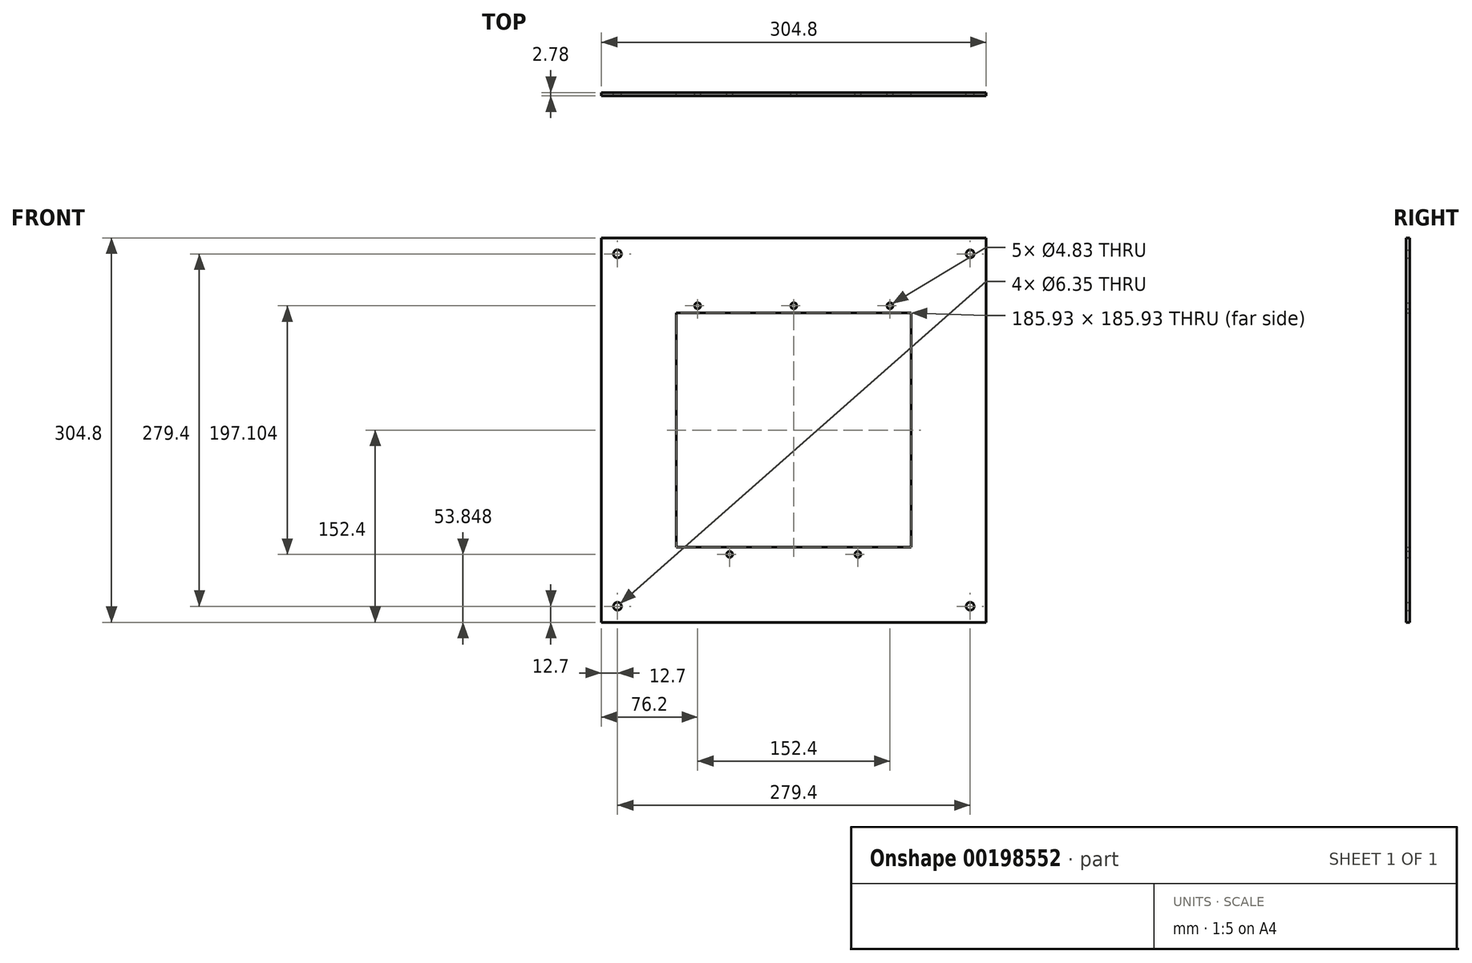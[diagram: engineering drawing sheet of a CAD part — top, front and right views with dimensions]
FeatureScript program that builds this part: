
annotation { "Feature Type Name" : "Feature", "Feature Type Description" : "" }
export const myFeature = defineFeature(function(context is Context, id is Id, definition is map)
    precondition{}
    {
        {
            var Q0;
            Q0=qCreatedBy(makeId("Front.planeOp"),FACE);
            var sketch = newSketch(context, id + "F0", { "sketchPlane" : qUnion([Q0])});
            skLineSegment(sketch, "E0.bottom", {"start": v(-152.4, 152.4) * mm, "end": v(152.4, 152.4) * mm});
            skLineSegment(sketch, "E0.top", {"start": v(-152.4, -152.4) * mm, "end": v(152.4, -152.4) * mm});
            skLineSegment(sketch, "E0.left", {"start": v(-152.4, 152.4) * mm, "end": v(-152.4, -152.4) * mm});
            skLineSegment(sketch, "E0.right", {"start": v(152.4, 152.4) * mm, "end": v(152.4, -152.4) * mm});
            skPoint(sketch, "E0.middle", {"position": v(0, 0) * mm});
            skLineSegment(sketch, "E1.bottom", {"start": v(-92.96, 92.96) * mm, "end": v(92.96, 92.96) * mm});
            skLineSegment(sketch, "E1.top", {"start": v(-92.96, -92.96) * mm, "end": v(92.96, -92.96) * mm});
            skLineSegment(sketch, "E1.left", {"start": v(-92.96, 92.96) * mm, "end": v(-92.96, -92.96) * mm});
            skLineSegment(sketch, "E1.right", {"start": v(92.96, 92.96) * mm, "end": v(92.96, -92.96) * mm});
            skCircle(sketch, "E2", {"center": v(0, 98.55) * mm, "radius": 2.41 * mm});
            skPoint(sketch, "E2.centerSnap0", {"position": v(0, 92.96) * mm});
            skCircle(sketch, "E3", {"center": v(76.2, 98.55) * mm, "radius": 2.41 * mm});
            skCircle(sketch, "E4", {"center": v(-76.2, 98.55) * mm, "radius": 2.41 * mm});
            skCircle(sketch, "E5", {"center": v(-50.8, -98.55) * mm, "radius": 2.41 * mm});
            skCircle(sketch, "E6", {"center": v(50.8, -98.55) * mm, "radius": 2.41 * mm});
            skCircle(sketch, "E7", {"center": v(-139.7, 139.7) * mm, "radius": 3.18 * mm});
            skCircle(sketch, "E8", {"center": v(139.7, 139.7) * mm, "radius": 3.18 * mm});
            skCircle(sketch, "E9", {"center": v(139.7, -139.7) * mm, "radius": 3.18 * mm});
            skCircle(sketch, "E10", {"center": v(-139.7, -139.7) * mm, "radius": 3.18 * mm});
            skSolve(sketch);
        }
        {
            var Q0;
            Q0 = qSketchRegion(id + "F0", true);
            extrude(context, id + "F1", {"entities" : qUnion([Q0]), "depth" : 2.78 * mm});
        }
    });
